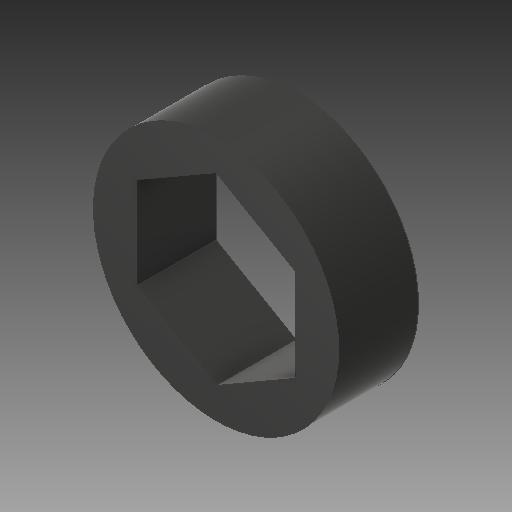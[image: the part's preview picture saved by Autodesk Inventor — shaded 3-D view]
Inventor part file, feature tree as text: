
AUTODESK INVENTOR PART (.ipt)
format: ipt  version: 2018 (Build 220112000, 112)  size: 100,864 bytes
history: native  units: in
note: dims shown in document units (in); Inventor stores cm internally (conversion verified against a paired STEP export)
features: extrude x1, sketch x1
ambient origin geometry x8: Origin, YZ Plane, XZ Plane, XY Plane, X Axis, Y Axis, Z Axis, Center Point
bodies: Solid1 (feature_tree)
feature tree (2):
  extrude  "Extrusion1"  Depth=0.25in
  sketch  "Sketch1"  dims[d0=0.5in d1=0.768in d2=0.25in d3=0.0in]
